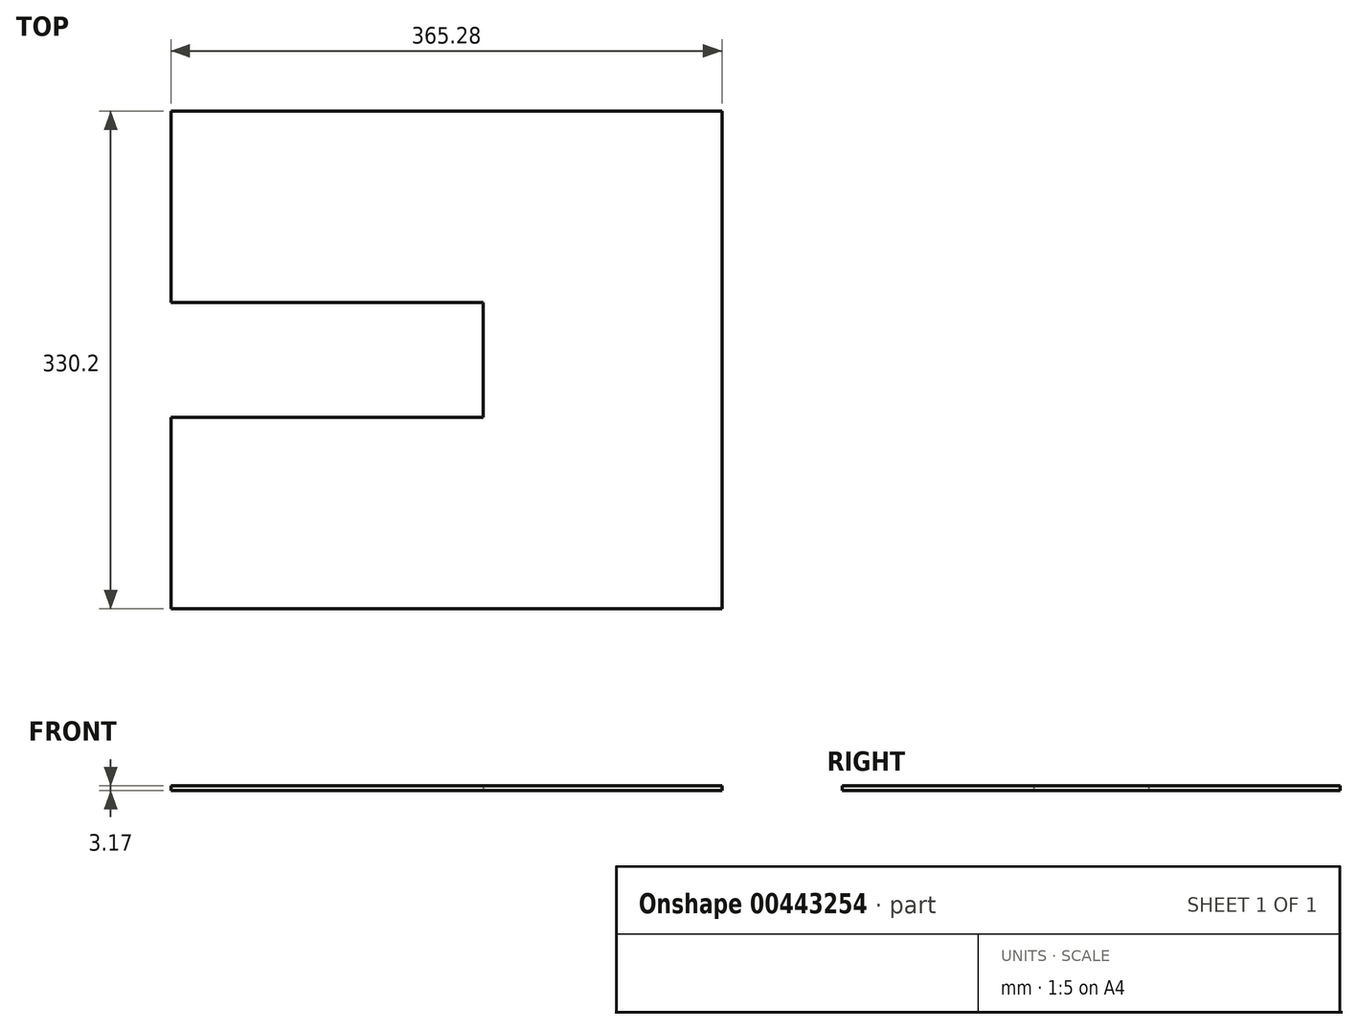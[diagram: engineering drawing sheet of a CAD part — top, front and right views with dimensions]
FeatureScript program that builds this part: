
annotation { "Feature Type Name" : "Feature", "Feature Type Description" : "" }
export const myFeature = defineFeature(function(context is Context, id is Id, definition is map)
    precondition{}
    {
        {
            var Q0;
            Q0=qCreatedBy(makeId("Top.planeOp"),FACE);
            var sketch = newSketch(context, id + "F0", { "sketchPlane" : qUnion([Q0])});
            skLineSegment(sketch, "E0.bottom", {"start": v(182.64, -165.1) * mm, "end": v(-182.64, -165.1) * mm});
            skLineSegment(sketch, "E0.top", {"start": v(182.64, 165.1) * mm, "end": v(-182.64, 165.1) * mm});
            skLineSegment(sketch, "E0.left", {"start": v(182.64, -165.1) * mm, "end": v(182.64, 165.1) * mm});
            skLineSegment(sketch, "E0.right", {"start": v(-182.64, -165.1) * mm, "end": v(-182.64, -77.42) * mm});
            skPoint(sketch, "E0.middle", {"position": v(0, 0) * mm});
            skPoint(sketch, "E1", {"position": v(-182.64, 0) * mm});
            skLineSegment(sketch, "E2.bottom", {"start": v(24.47, -38.1) * mm, "end": v(-182.64, -38.1) * mm});
            skLineSegment(sketch, "E2.top", {"start": v(24.47, 38.1) * mm, "end": v(-182.64, 38.1) * mm});
            skLineSegment(sketch, "E2.left", {"start": v(24.47, -38.1) * mm, "end": v(24.47, 38.1) * mm});
            skLineSegment(sketch, "E3", {"start": v(-182.64, 38.1) * mm, "end": v(-182.64, 165.1) * mm});
            skLineSegment(sketch, "E4", {"start": v(-182.64, -77.42) * mm, "end": v(-182.64, 38.1) * mm});
            skSolve(sketch);
        }
        {
            var Q0;
            Q0=makeQuery(id+"F0.imprint","IMPRINT",FACE,{"disambiguationData":[TD([[makeQuery(id+"F0.imprint","IMPRINT",EDGE,{"derivedFrom":sQuery(id+"F0.wireOp",EDGE,"E0.bottom")}),-1.0]])]});
            extrude(context, id + "F1", {"entities" : qUnion([Q0]), "depth" : 3.17 * mm, "offsetDistance" : 25.4 * mm});
        }
    });
